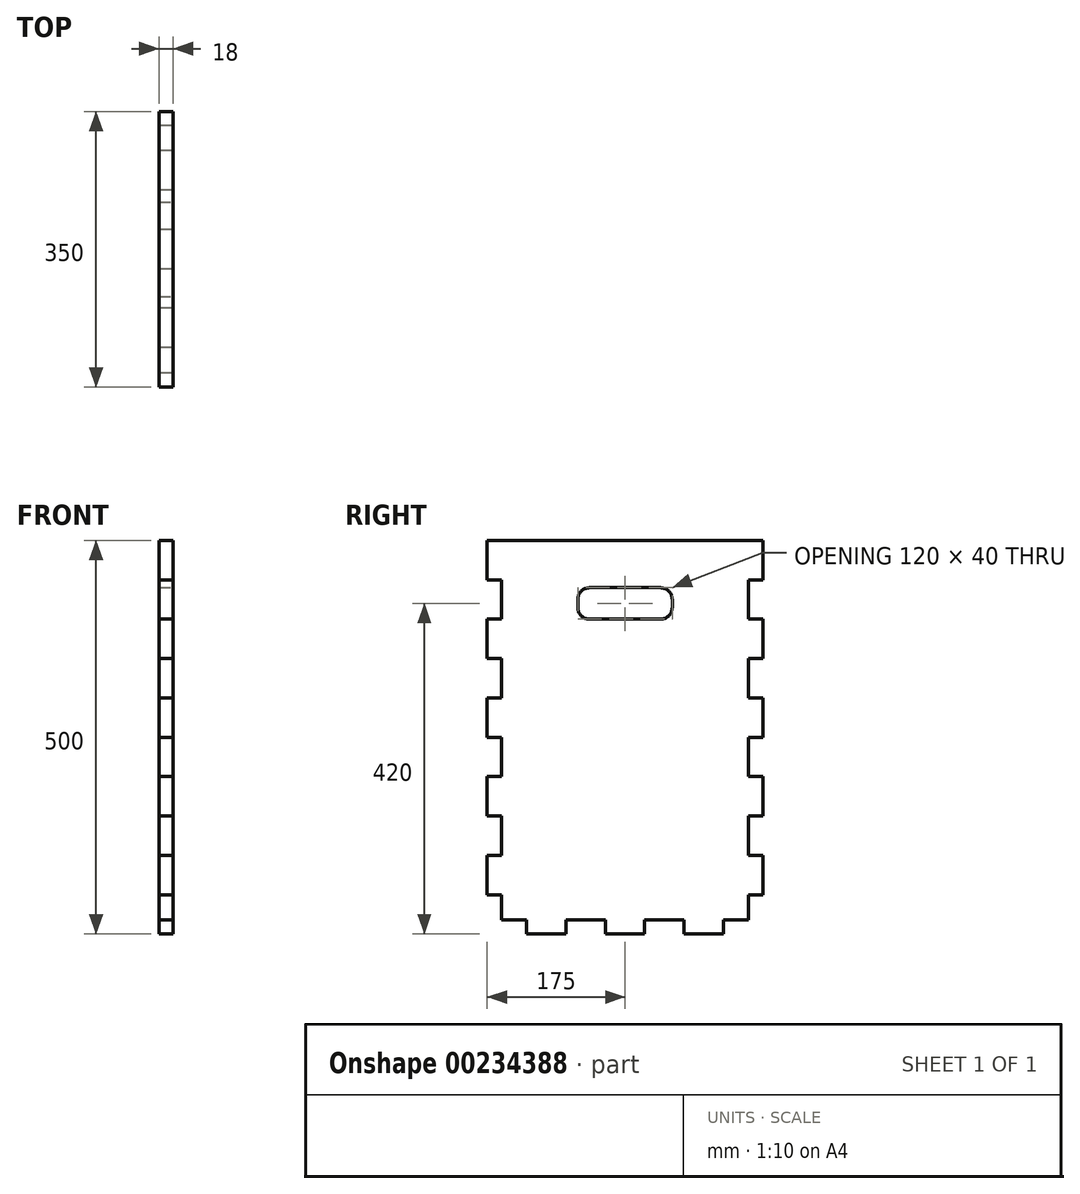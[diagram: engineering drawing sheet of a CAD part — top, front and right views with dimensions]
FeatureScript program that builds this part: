
annotation { "Feature Type Name" : "Feature", "Feature Type Description" : "" }
export const myFeature = defineFeature(function(context is Context, id is Id, definition is map)
    precondition{}
    {
        {
            var Q0;
            Q0=qCreatedBy(makeId("Right.planeOp"),FACE);
            var sketch = newSketch(context, id + "F0", { "sketchPlane" : qUnion([Q0])});
            skLineSegment(sketch, "E0.bottom", {"start": v(-175, 250) * mm, "end": v(175, 250) * mm});
            skLineSegment(sketch, "E0.top", {"start": v(-125, -250) * mm, "end": v(-75, -250) * mm});
            skLineSegment(sketch, "E0.left", {"start": v(-175, 250) * mm, "end": v(-175, 200) * mm});
            skLineSegment(sketch, "E0.right", {"start": v(175, 250) * mm, "end": v(175, 200) * mm});
            skPoint(sketch, "E0.middle", {"position": v(0, 0) * mm});
            skLineSegment(sketch, "E1.top", {"start": v(157, -232) * mm, "end": v(125, -232) * mm});
            skLineSegment(sketch, "E1.right", {"start": v(125, -250) * mm, "end": v(125, -232) * mm});
            skLineSegment(sketch, "E2.top", {"start": v(125, -250) * mm, "end": v(75, -250) * mm});
            skLineSegment(sketch, "E2.left", {"start": v(125, -232) * mm, "end": v(125, -250) * mm});
            skLineSegment(sketch, "E2.right", {"start": v(75, -232) * mm, "end": v(75, -250) * mm});
            skLineSegment(sketch, "E3.bottom", {"start": v(75, -232) * mm, "end": v(25, -232) * mm});
            skLineSegment(sketch, "E3.right", {"start": v(25, -232) * mm, "end": v(25, -250) * mm});
            skLineSegment(sketch, "E4.top", {"start": v(25, -250) * mm, "end": v(-25, -250) * mm});
            skLineSegment(sketch, "E4.right", {"start": v(-25, -232) * mm, "end": v(-25, -250) * mm});
            skLineSegment(sketch, "E5.bottom", {"start": v(-25, -232) * mm, "end": v(-75, -232) * mm});
            skLineSegment(sketch, "E5.right", {"start": v(-75, -232) * mm, "end": v(-75, -250) * mm});
            skLineSegment(sketch, "E6.top", {"start": v(-75, -250) * mm, "end": v(-125, -250) * mm});
            skLineSegment(sketch, "E6.right", {"start": v(-125, -232) * mm, "end": v(-125, -250) * mm});
            skLineSegment(sketch, "E7.bottom", {"start": v(-125, -232) * mm, "end": v(-157, -232) * mm});
            skPoint(sketch, "E8.orphan", {"position": v(175, -250) * mm});
            skLineSegment(sketch, "E9.trimOffspring", {"start": v(75, -250) * mm, "end": v(125, -250) * mm});
            skLineSegment(sketch, "E10.trimOffspring", {"start": v(-25, -250) * mm, "end": v(25, -250) * mm});
            skPoint(sketch, "E11.orphan", {"position": v(-175, -250) * mm});
            skLineSegment(sketch, "E12.top", {"start": v(-175, -200) * mm, "end": v(-157, -200) * mm});
            skLineSegment(sketch, "E12.right", {"start": v(-157, -232) * mm, "end": v(-157, -200) * mm});
            skLineSegment(sketch, "E13.bottom", {"start": v(-157, -200) * mm, "end": v(-175, -200) * mm});
            skLineSegment(sketch, "E13.top", {"start": v(-157, -150) * mm, "end": v(-175, -150) * mm});
            skLineSegment(sketch, "E13.right", {"start": v(-175, -200) * mm, "end": v(-175, -150) * mm});
            skLineSegment(sketch, "E14.top", {"start": v(-157, -100) * mm, "end": v(-175, -100) * mm});
            skLineSegment(sketch, "E14.left", {"start": v(-157, -150) * mm, "end": v(-157, -100) * mm});
            skLineSegment(sketch, "E15.top", {"start": v(-157, -50) * mm, "end": v(-175, -50) * mm});
            skLineSegment(sketch, "E15.right", {"start": v(-175, -100) * mm, "end": v(-175, -50) * mm});
            skLineSegment(sketch, "E16.top", {"start": v(-157, 0) * mm, "end": v(-175, 0) * mm});
            skLineSegment(sketch, "E16.left", {"start": v(-157, -50) * mm, "end": v(-157, 0) * mm});
            skLineSegment(sketch, "E17.top", {"start": v(-157, 50) * mm, "end": v(-175, 50) * mm});
            skLineSegment(sketch, "E17.right", {"start": v(-175, 0) * mm, "end": v(-175, 50) * mm});
            skLineSegment(sketch, "E18.top", {"start": v(-157, 100) * mm, "end": v(-175, 100) * mm});
            skLineSegment(sketch, "E18.left", {"start": v(-157, 50) * mm, "end": v(-157, 100) * mm});
            skLineSegment(sketch, "E19.top", {"start": v(-157, 150) * mm, "end": v(-175, 150) * mm});
            skLineSegment(sketch, "E19.right", {"start": v(-175, 100) * mm, "end": v(-175, 150) * mm});
            skLineSegment(sketch, "E20.top", {"start": v(-157, 200) * mm, "end": v(-175, 200) * mm});
            skLineSegment(sketch, "E20.left", {"start": v(-157, 150) * mm, "end": v(-157, 200) * mm});
            skLineSegment(sketch, "E21.top", {"start": v(-157, 250) * mm, "end": v(-175, 250) * mm});
            skLineSegment(sketch, "E21.right", {"start": v(-175, 200) * mm, "end": v(-175, 250) * mm});
            skLineSegment(sketch, "E22.trimOffspring", {"start": v(-175, -150) * mm, "end": v(-175, -200) * mm});
            skLineSegment(sketch, "E23.trimOffspring", {"start": v(-175, -50) * mm, "end": v(-175, -100) * mm});
            skLineSegment(sketch, "E24.trimOffspring", {"start": v(-175, 50) * mm, "end": v(-175, 0) * mm});
            skLineSegment(sketch, "E25.trimOffspring", {"start": v(-175, 150) * mm, "end": v(-175, 100) * mm});
            skLineSegment(sketch, "E26.bottom", {"start": v(175, 250) * mm, "end": v(157, 250) * mm});
            skLineSegment(sketch, "E26.top", {"start": v(175, 200) * mm, "end": v(157, 200) * mm});
            skLineSegment(sketch, "E27.bottom", {"start": v(157, 200) * mm, "end": v(175, 200) * mm});
            skLineSegment(sketch, "E27.top", {"start": v(157, 150) * mm, "end": v(175, 150) * mm});
            skLineSegment(sketch, "E27.left", {"start": v(157, 200) * mm, "end": v(157, 150) * mm});
            skLineSegment(sketch, "E28.top", {"start": v(157, 100) * mm, "end": v(175, 100) * mm});
            skLineSegment(sketch, "E28.right", {"start": v(175, 150) * mm, "end": v(175, 100) * mm});
            skLineSegment(sketch, "E29.top", {"start": v(157, 50) * mm, "end": v(175, 50) * mm});
            skLineSegment(sketch, "E29.left", {"start": v(157, 100) * mm, "end": v(157, 50) * mm});
            skLineSegment(sketch, "E30.top", {"start": v(157, 0) * mm, "end": v(175, 0) * mm});
            skLineSegment(sketch, "E30.right", {"start": v(175, 50) * mm, "end": v(175, 0) * mm});
            skLineSegment(sketch, "E31.top", {"start": v(157, -50) * mm, "end": v(175, -50) * mm});
            skLineSegment(sketch, "E31.left", {"start": v(157, 0) * mm, "end": v(157, -50) * mm});
            skLineSegment(sketch, "E32.top", {"start": v(157, -100) * mm, "end": v(175, -100) * mm});
            skLineSegment(sketch, "E32.right", {"start": v(175, -50) * mm, "end": v(175, -100) * mm});
            skLineSegment(sketch, "E33.top", {"start": v(157, -150) * mm, "end": v(175, -150) * mm});
            skLineSegment(sketch, "E33.left", {"start": v(157, -100) * mm, "end": v(157, -150) * mm});
            skLineSegment(sketch, "E34.right", {"start": v(175, -150) * mm, "end": v(175, -200) * mm});
            skLineSegment(sketch, "E35.bottom", {"start": v(175, -200) * mm, "end": v(157, -200) * mm});
            skLineSegment(sketch, "E35.right", {"start": v(157, -200) * mm, "end": v(157, -232) * mm});
            skSolve(sketch);
        }
        {
            var Q0;
            Q0 = qSketchRegion(id + "F0", true);
            extrude(context, id + "F1", {"entities" : qUnion([Q0]), "depth" : 18 * mm});
        }
        {
            var Q0;
            Q0=makeQuery(id+"F1.opExtrude","CAP_FACE",FACE,{"disambiguationData":[OSD([sQuery(id+"F0.wireOp",EDGE,"E0.bottom"),sQuery(id+"F0.wireOp",EDGE,"E1.top"),sQuery(id+"F0.wireOp",EDGE,"E2.left"),sQuery(id+"F0.wireOp",EDGE,"E3.bottom"),sQuery(id+"F0.wireOp",EDGE,"E2.right"),sQuery(id+"F0.wireOp",EDGE,"E3.right"),sQuery(id+"F0.wireOp",EDGE,"E5.bottom"),sQuery(id+"F0.wireOp",EDGE,"E4.right"),sQuery(id+"F0.wireOp",EDGE,"E6.top"),sQuery(id+"F0.wireOp",EDGE,"E5.right"),sQuery(id+"F0.wireOp",EDGE,"E7.bottom"),sQuery(id+"F0.wireOp",EDGE,"E6.right"),sQuery(id+"F0.wireOp",EDGE,"E9.trimOffspring"),sQuery(id+"F0.wireOp",EDGE,"E10.trimOffspring"),sQuery(id+"F0.wireOp",EDGE,"E12.right"),sQuery(id+"F0.wireOp",EDGE,"E13.bottom"),sQuery(id+"F0.wireOp",EDGE,"E13.top"),sQuery(id+"F0.wireOp",EDGE,"E14.left"),sQuery(id+"F0.wireOp",EDGE,"E14.top"),sQuery(id+"F0.wireOp",EDGE,"E15.top"),sQuery(id+"F0.wireOp",EDGE,"E16.left"),sQuery(id+"F0.wireOp",EDGE,"E16.top"),sQuery(id+"F0.wireOp",EDGE,"E17.top"),sQuery(id+"F0.wireOp",EDGE,"E18.left"),sQuery(id+"F0.wireOp",EDGE,"E18.top"),sQuery(id+"F0.wireOp",EDGE,"E19.top"),sQuery(id+"F0.wireOp",EDGE,"E20.left"),sQuery(id+"F0.wireOp",EDGE,"E20.top"),sQuery(id+"F0.wireOp",EDGE,"E21.top"),sQuery(id+"F0.wireOp",EDGE,"E21.right"),sQuery(id+"F0.wireOp",EDGE,"E22.trimOffspring"),sQuery(id+"F0.wireOp",EDGE,"E23.trimOffspring"),sQuery(id+"F0.wireOp",EDGE,"E24.trimOffspring"),sQuery(id+"F0.wireOp",EDGE,"E25.trimOffspring"),sQuery(id+"F0.wireOp",EDGE,"E26.bottom"),sQuery(id+"F0.wireOp",EDGE,"E0.right"),sQuery(id+"F0.wireOp",EDGE,"E27.bottom"),sQuery(id+"F0.wireOp",EDGE,"E27.left"),sQuery(id+"F0.wireOp",EDGE,"E27.top"),sQuery(id+"F0.wireOp",EDGE,"E28.top"),sQuery(id+"F0.wireOp",EDGE,"E29.left"),sQuery(id+"F0.wireOp",EDGE,"E29.top"),sQuery(id+"F0.wireOp",EDGE,"E30.top"),sQuery(id+"F0.wireOp",EDGE,"E31.left"),sQuery(id+"F0.wireOp",EDGE,"E31.top"),sQuery(id+"F0.wireOp",EDGE,"E32.top"),sQuery(id+"F0.wireOp",EDGE,"E33.left"),sQuery(id+"F0.wireOp",EDGE,"E33.top"),sQuery(id+"F0.wireOp",EDGE,"E34.right"),sQuery(id+"F0.wireOp",EDGE,"E32.right"),sQuery(id+"F0.wireOp",EDGE,"E30.right"),sQuery(id+"F0.wireOp",EDGE,"E28.right"),sQuery(id+"F0.wireOp",EDGE,"E35.bottom"),sQuery(id+"F0.wireOp",EDGE,"E35.right")])],"isStart":false});
            var sketch = newSketch(context, id + "F2", { "sketchPlane" : qUnion([Q0])});
            skLineSegment(sketch, "E36.bottom", {"start": v(-45, 190) * mm, "end": v(45, 190) * mm});
            skLineSegment(sketch, "E36.top", {"start": v(-45, 150) * mm, "end": v(45, 150) * mm});
            skLineSegment(sketch, "E36.left", {"start": v(-60, 175) * mm, "end": v(-60, 165) * mm});
            skLineSegment(sketch, "E36.right", {"start": v(60, 175) * mm, "end": v(60, 165) * mm});
            skPoint(sketch, "E36.middle", {"position": v(0, 170) * mm});
            skPoint(sketch, "E37.visualSharp", {"position": v(-60, 190) * mm});
            skArc(sketch, "E37.filletArc", {"start": v(-45, 190) * mm, "mid": v(-55.6, 185.6) * mm, "end": v(-60, 175) * mm});
            skPoint(sketch, "E38.visualSharp", {"position": v(60, 190) * mm});
            skArc(sketch, "E38.filletArc", {"start": v(60, 175) * mm, "mid": v(55.6, 185.6) * mm, "end": v(45, 190) * mm});
            skPoint(sketch, "E39.visualSharp", {"position": v(60, 150) * mm});
            skArc(sketch, "E39.filletArc", {"start": v(45, 150) * mm, "mid": v(55.6, 154.4) * mm, "end": v(60, 165) * mm});
            skPoint(sketch, "E40.visualSharp", {"position": v(-60, 150) * mm});
            skArc(sketch, "E40.filletArc", {"start": v(-60, 165) * mm, "mid": v(-55.6, 154.4) * mm, "end": v(-45, 150) * mm});
            skSolve(sketch);
        }
        {
            var Q0;
            Q0 = qSketchRegion(id + "F2", true);
            extrude(context, id + "F3", {"entities" : qUnion([Q0]), "operationType" : NewBodyOperationType.REMOVE, "oppositeDirection" : true, "depth" : 25 * mm});
        }
    });
